# Revit family: Projector_Mount-Ceiling-Chief-RPMx
name_source: partatom
category: Specialty Equipment
revit_build: Autodesk Revit Structure 2012 (Build: 20110916_2132(x64)
units: mm (PartAtom-declared; Revit-internal decimal feet)

## types (3) — shared parameters
04 CSI = 11 52 00
95 CSI = 11130
Assembly Code = E1020500
CAD Drawings URL = http://downloads.chiefmfg.com
Certification = TÜV Certified, UL Listed
Cost Info = http://www.chiefmfg.com
Default Elevation = 4' - 0"
Description = Projector Ceiling Mount
Height = 0' - 5 1/2"
Length = 0' - 2 23/32"
Manual and Installation URL = http://downloads.chiefmfg.com
Manufacturer = Chief
Manufacturer Fax = 877.894.6918
Pitch Range = 20°
Product Line = RPMx
Product Page URL = http://www.chiefmfg.com
Roll Range = 3°
Subcategory = Projector Ceiling Mounts
URL = http://www.chiefmfg.com
Weight Capacity = 50.00 lb
Width = 0' - 6 1/2"
Yaw Range = 360°
ecoScorecard Product Page = http://ecoscorecard.com

## per-type parameters (varying)
| type | Material Finish | Product Color |
| RPMAU | Metal - Chief - Black | Black |
| RPMAUS | Metal - Chief - Silver | Silver |
| RPMAUW | Metal - Chief - White | White |

note: column(s) folded — value = type name in every type: Model

## geometry (parser evidence)
native form markers: Blend x6, Sweep x2
no freeform markers — native parametric forms only
